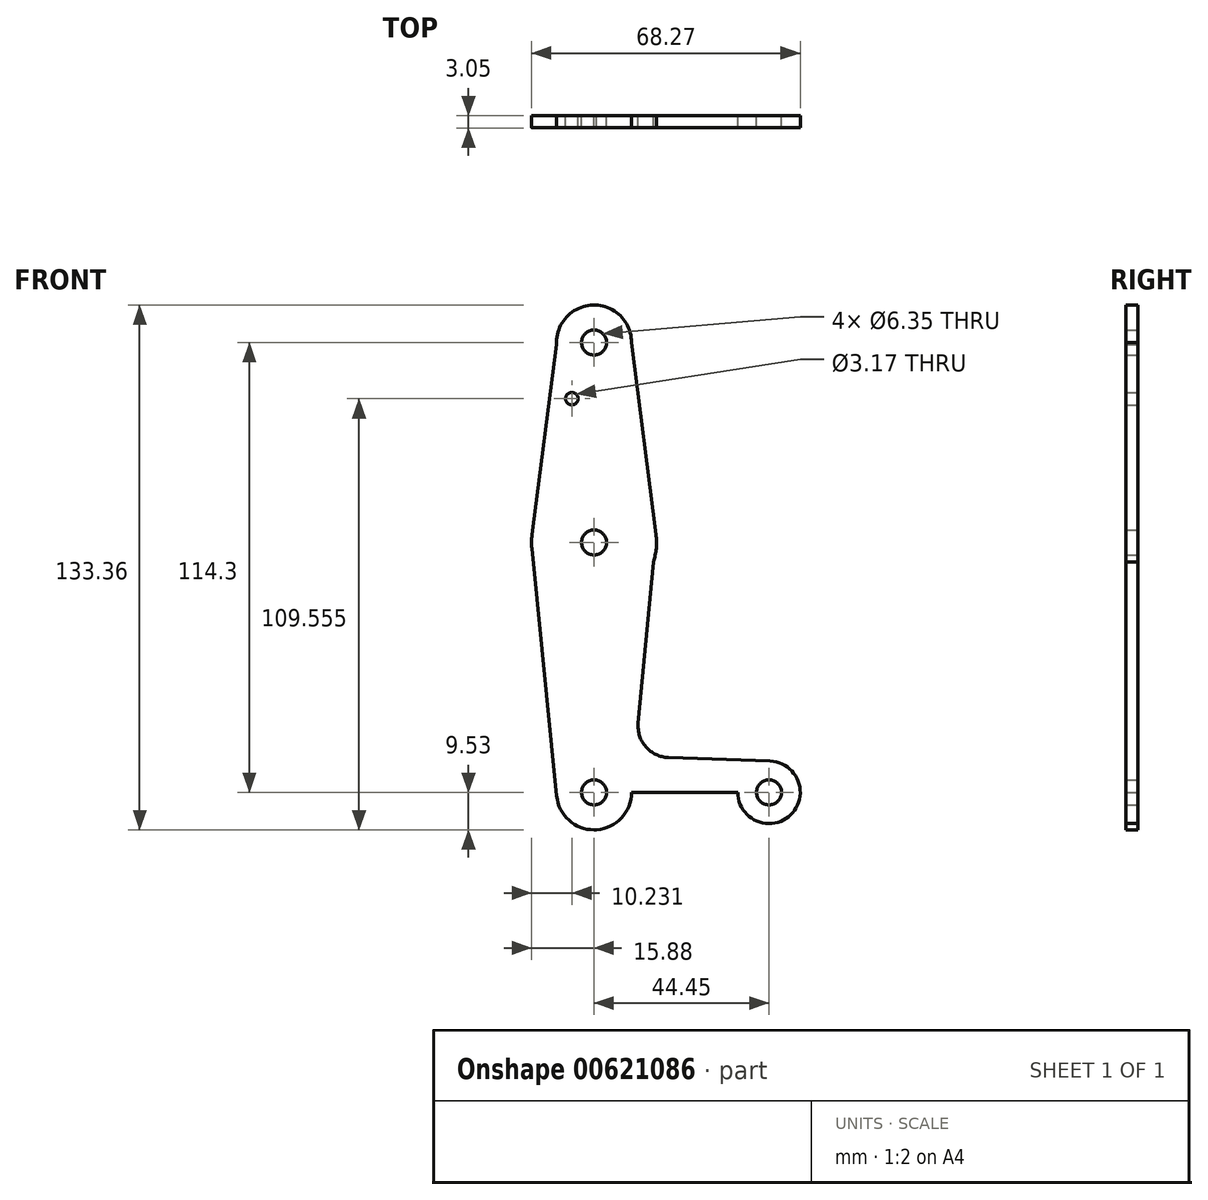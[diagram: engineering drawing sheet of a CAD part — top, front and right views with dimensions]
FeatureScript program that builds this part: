
annotation { "Feature Type Name" : "Feature", "Feature Type Description" : "" }
export const myFeature = defineFeature(function(context is Context, id is Id, definition is map)
    precondition{}
    {
        {
            var Q0;
            Q0=qCreatedBy(makeId("Front.planeOp"),FACE);
            var sketch = newSketch(context, id + "F0", { "sketchPlane" : qUnion([Q0])});
            skLineSegment(sketch, "E0", {"start": v(0, 0) * mm, "end": v(0, 63.5) * mm});
            skCircle(sketch, "E1", {"center": v(0, 63.5) * mm, "radius": 15.88 * mm});
            skLineSegment(sketch, "E2", {"start": v(0, 63.5) * mm, "end": v(0, 114.3) * mm});
            skCircle(sketch, "E3", {"center": v(0, 0) * mm, "radius": 9.53 * mm});
            skCircle(sketch, "E4", {"center": v(0, 114.3) * mm, "radius": 9.53 * mm});
            skLineSegment(sketch, "E5", {"start": v(0, 0) * mm, "end": v(44.45, 0) * mm});
            skCircle(sketch, "E6", {"center": v(44.45, 0) * mm, "radius": 7.94 * mm});
            skLineSegment(sketch, "E7", {"start": v(-9.51, 113.78) * mm, "end": v(-15.74, 65.53) * mm});
            skLineSegment(sketch, "E8", {"start": v(9.53, 114.3) * mm, "end": v(15.75, 65.5) * mm});
            skLineSegment(sketch, "E9", {"start": v(15.75, 65.5) * mm, "end": v(11.22, 17.55) * mm});
            skLineSegment(sketch, "E10", {"start": v(18.85, 8.85) * mm, "end": v(44.73, 7.93) * mm});
            skLineSegment(sketch, "E11", {"start": v(0, -9.53) * mm, "end": v(44.73, -7.93) * mm});
            skPoint(sketch, "E12.newPointA", {"position": v(9.57, 0) * mm});
            skArc(sketch, "E12.filletArc", {"start": v(11.22, 17.55) * mm, "mid": v(13.16, 11.55) * mm, "end": v(18.85, 8.85) * mm});
            skCircle(sketch, "E13", {"center": v(0, 114.3) * mm, "radius": 3.18 * mm});
            skCircle(sketch, "E14", {"center": v(-5.65, 100.03) * mm, "radius": 1.59 * mm});
            skCircle(sketch, "E15", {"center": v(0, 63.5) * mm, "radius": 3.18 * mm});
            skCircle(sketch, "E16", {"center": v(0, 0) * mm, "radius": 3.18 * mm});
            skCircle(sketch, "E17", {"center": v(44.45, 0) * mm, "radius": 3.18 * mm});
            skLineSegment(sketch, "E18", {"start": v(-15.8, 61.91) * mm, "end": v(-9.48, -0.95) * mm});
            skSolve(sketch);
        }
        {
            var Q0;
            {var subQ0=sQuery(id+"F0.wireOp",EDGE,"kogNqwxc-1IiU-YP61-FTKE-ky83wEDOdzxT");var subQ1=sQuery(id+"F0.wireOp",EDGE,"E1");var subQ2=makeQuery(id+"F0.imprint","INTERSECT",VERTEX,{"disambiguationData":[OD(0.0)],"derivedFrom":[subQ1,subQ0]});Q0=makeQuery(id+"F0.imprint","IMPRINT",FACE,{"disambiguationData":[TD([[makeQuery(id+"F0.imprint","IMPRINT",EDGE,{"disambiguationData":[TD([[subQ2,-1.0]])],"derivedFrom":subQ1}),1.0]])]});}
            var Q1;
            {var subQ0=sQuery(id+"F0.wireOp",EDGE,"E9");var subQ1=sQuery(id+"F0.wireOp",EDGE,"E1");var subQ3=makeQuery(id+"F0.imprint","INTERSECT",VERTEX,{"derivedFrom":[subQ1,subQ0]});Q1=makeQuery(id+"F0.imprint","IMPRINT",FACE,{"disambiguationData":[TD([[makeQuery(id+"F0.imprint","IMPRINT",EDGE,{"disambiguationData":[TD([[subQ3,-1.0]])],"derivedFrom":subQ1}),1.0]])]});}
            var Q2;
            {var subQ0=sQuery(id+"F0.wireOp",EDGE,"E11");var subQ1=sQuery(id+"F0.wireOp",EDGE,"E3");var subQ2=makeQuery(id+"F0.imprint","INTERSECT",VERTEX,{"disambiguationData":[OD(0.0)],"derivedFrom":[subQ1,subQ0]});Q2=makeQuery(id+"F0.imprint","IMPRINT",FACE,{"disambiguationData":[TD([[makeQuery(id+"F0.imprint","IMPRINT",EDGE,{"disambiguationData":[TD([[subQ2,-1.0]])],"derivedFrom":subQ1}),1.0]])]});}
            var Q3;
            {var subQ0=sQuery(id+"F0.wireOp",EDGE,"E3");var subQ1=sQuery(id+"F0.wireOp",EDGE,"E0");var subQ2=makeQuery(id+"F0.imprint","INTERSECT",VERTEX,{"derivedFrom":[subQ1,subQ0]});Q3=makeQuery(id+"F0.imprint","IMPRINT",FACE,{"disambiguationData":[TD([[makeQuery(id+"F0.imprint","IMPRINT",EDGE,{"disambiguationData":[TD([[subQ2,1.0]])],"derivedFrom":subQ1}),-1.0]])]});}
            var Q4;
            {var subQ0=sQuery(id+"F0.wireOp",EDGE,"E8");Q4=makeQuery(id+"F0.imprint","IMPRINT",FACE,{"disambiguationData":[TD([[makeQuery(id+"F0.imprint","IMPRINT",EDGE,{"derivedFrom":subQ0}),-1.0]])]});}
            var Q5;
            {var subQ0=sQuery(id+"F0.wireOp",EDGE,"E11");var subQ1=sQuery(id+"F0.wireOp",EDGE,"E3");var subQ2=makeQuery(id+"F0.imprint","INTERSECT",VERTEX,{"disambiguationData":[OD(1.0)],"derivedFrom":[subQ1,subQ0]});Q5=makeQuery(id+"F0.imprint","IMPRINT",FACE,{"disambiguationData":[TD([[makeQuery(id+"F0.imprint","IMPRINT",EDGE,{"disambiguationData":[TD([[subQ2,-1.0]])],"derivedFrom":subQ1}),-1.0]])]});}
            var Q6;
            Q6=makeQuery(id+"F0.imprint","IMPRINT",FACE,{"disambiguationData":[TD([[makeQuery(id+"F0.imprint","IMPRINT",EDGE,{"derivedFrom":sQuery(id+"F0.wireOp",EDGE,"E13")}),-1.0]])]});
            var Q7;
            Q7=makeQuery(id+"F0.imprint","IMPRINT",FACE,{"disambiguationData":[TD([[makeQuery(id+"F0.imprint","IMPRINT",EDGE,{"derivedFrom":sQuery(id+"F0.wireOp",EDGE,"E17")}),-1.0]])]});
            var Q8;
            {var subQ1=sQuery(id+"F0.wireOp",EDGE,"E3");var subQ5=sQuery(id+"F0.wireOp",EDGE,"E0");var subQ6=makeQuery(id+"F0.imprint","INTERSECT",VERTEX,{"derivedFrom":[subQ5,subQ1]});Q8=makeQuery(id+"F0.imprint","IMPRINT",FACE,{"disambiguationData":[TD([[makeQuery(id+"F0.imprint","IMPRINT",EDGE,{"disambiguationData":[TD([[subQ6,1.0]])],"derivedFrom":subQ5}),1.0]])]});}
            var Q9;
            {var subQ12=sQuery(id+"F0.wireOp",EDGE,"E10");Q9=makeQuery(id+"F0.imprint","IMPRINT",FACE,{"disambiguationData":[TD([[makeQuery(id+"F0.imprint","IMPRINT",EDGE,{"derivedFrom":subQ12}),-1.0]])]});}
            var Q10;
            {var subQ1=sQuery(id+"F0.wireOp",EDGE,"E1");var subQ3=sQuery(id+"F0.wireOp",EDGE,"E0");var subQ4=makeQuery(id+"F0.imprint","INTERSECT",VERTEX,{"derivedFrom":[subQ3,subQ1]});Q10=makeQuery(id+"F0.imprint","IMPRINT",FACE,{"disambiguationData":[TD([[makeQuery(id+"F0.imprint","IMPRINT",EDGE,{"disambiguationData":[TD([[subQ4,-1.0]])],"derivedFrom":subQ3}),1.0]])]});}
            var Q11;
            {var subQ0=sQuery(id+"F0.wireOp",EDGE,"E7");Q11=makeQuery(id+"F0.imprint","IMPRINT",FACE,{"disambiguationData":[TD([[makeQuery(id+"F0.imprint","IMPRINT",EDGE,{"derivedFrom":subQ0}),1.0]])]});}
            var Q12;
            {var subQ0=sQuery(id+"F0.wireOp",EDGE,"E1");var subQ1=sQuery(id+"F0.wireOp",EDGE,"E0");var subQ2=makeQuery(id+"F0.imprint","INTERSECT",VERTEX,{"derivedFrom":[subQ1,subQ0]});Q12=makeQuery(id+"F0.imprint","IMPRINT",FACE,{"disambiguationData":[TD([[makeQuery(id+"F0.imprint","IMPRINT",EDGE,{"disambiguationData":[TD([[subQ2,-1.0]])],"derivedFrom":subQ1}),-1.0]])]});}
            var Q13;
            {var subQ5=sQuery(id+"F0.wireOp",EDGE,"E18");Q13=makeQuery(id+"F0.imprint","IMPRINT",FACE,{"disambiguationData":[TD([[makeQuery(id+"F0.imprint","IMPRINT",EDGE,{"derivedFrom":subQ5}),1.0]])]});}
            extrude(context, id + "F1", {"entities" : qUnion([Q0, Q1, Q2, Q3, Q4, Q5, Q6, Q7, Q8, Q9, Q10, Q11, Q12, Q13]), "depth" : 3.05 * mm, "offsetDistance" : 25.4 * mm});
        }
    });
